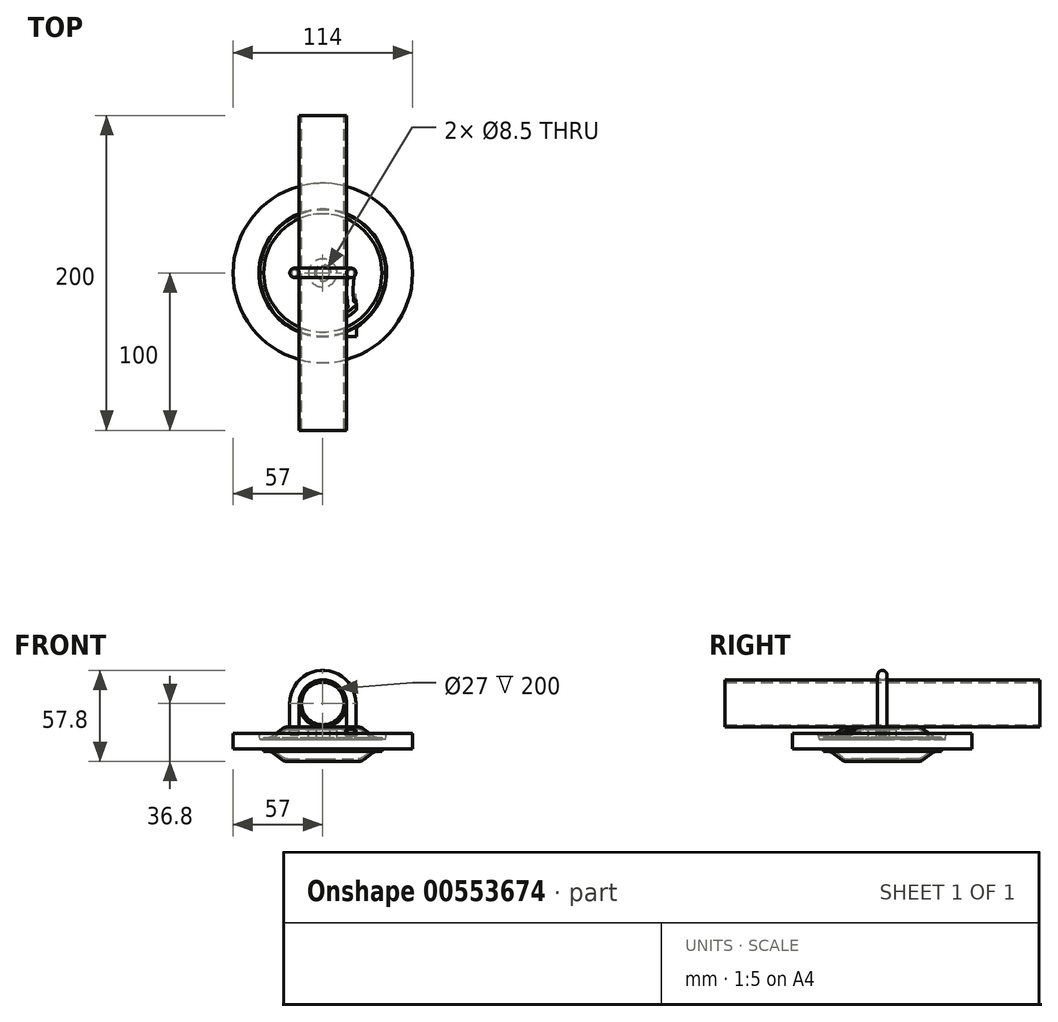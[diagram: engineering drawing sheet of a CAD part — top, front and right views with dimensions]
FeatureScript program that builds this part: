
annotation { "Feature Type Name" : "Feature", "Feature Type Description" : "" }
export const myFeature = defineFeature(function(context is Context, id is Id, definition is map)
    precondition{}
    {
        {
            assignVariable(context, id + "F0", {"name" : "ClampBolzen", "anyValue" : 4});
        }
        {
            var Q0;
            Q0=qCreatedBy(makeId("Front.planeOp"),FACE);
            var sketch = newSketch(context, id + "F1", { "sketchPlane" : qUnion([Q0])});
            skLineSegment(sketch, "E0", {"start": v(0, 0) * mm, "end": v(0, 76.33) * mm, "construction": true});
            skLineSegment(sketch, "E1", {"start": v(0, 0) * mm, "end": v(40, 0) * mm});
            skLineSegment(sketch, "E2", {"start": v(40, 0) * mm, "end": v(40.48, 3.9) * mm});
            skLineSegment(sketch, "E3", {"start": v(40.48, 3.9) * mm, "end": v(57, 3.9) * mm});
            skLineSegment(sketch, "E4", {"start": v(57, 3.9) * mm, "end": v(57, -6) * mm});
            skLineSegment(sketch, "E5", {"start": v(57, -6) * mm, "end": v(0, -6) * mm});
            skLineSegment(sketch, "E6", {"start": v(0, -6) * mm, "end": v(0, 0) * mm});
            skPoint(sketch, "E7", {"position": v(0, -3) * mm});
            skSolve(sketch);
        }
        {
            var Q0;
            Q0=qSketchRegion(id+"F1",true);
            var Q1;
            Q1=sQuery(id+"F1.wireOp",EDGE,"E0");
            revolve(context, id + "F2", {"entities" : qUnion([Q0]), "axis" : qUnion([Q1]), "revolveType" : RevolveType.FULL});
        }
        {
            var Q0;
            Q0=qCreatedBy(makeId("Front.planeOp"),FACE);
            var sketch = newSketch(context, id + "F3", { "sketchPlane" : qUnion([Q0])});
            skCircle(sketch, "E8", {"center": v(0, 22.9) * mm, "radius": 15 * mm});
            skCircle(sketch, "E9", {"center": v(0, 22.9) * mm, "radius": 13.5 * mm});
            skSolve(sketch);
        }
        {
            var Q0;
            Q0=qSketchRegion(id+"F3",true);
            extrude(context, id + "F4", {"entities" : qUnion([Q0]), "endBound" : BoundingType.SYMMETRIC, "depth" : 200 * mm, "offsetDistance" : 25 * mm});
        }
        {
            var Q0;
            Q0=qCreatedBy(makeId("Front.planeOp"),FACE);
            var sketch = newSketch(context, id + "F5", { "sketchPlane" : qUnion([Q0])});
            skLineSegment(sketch, "E10", {"start": v(0, -22.63) * mm, "end": v(0, 22.63) * mm, "construction": true});
            skLineSegment(sketch, "E11", {"start": v(4.25, 7.9) * mm, "end": v(24.5, 7.9) * mm});
            skLineSegment(sketch, "E12", {"start": v(24.5, 7.9) * mm, "end": v(33, 1.5) * mm});
            skLineSegment(sketch, "E13", {"start": v(33, 1.5) * mm, "end": v(37.5, 1.5) * mm});
            skLineSegment(sketch, "E14.0", {"start": v(32.5, 0) * mm, "end": v(37.5, 0) * mm});
            skLineSegment(sketch, "E14.1", {"start": v(24, 6.4) * mm, "end": v(32.5, 0) * mm});
            skLineSegment(sketch, "E14.2", {"start": v(4.25, 6.4) * mm, "end": v(24, 6.4) * mm});
            skLineSegment(sketch, "E15", {"start": v(37.5, 1.5) * mm, "end": v(37.5, 0) * mm});
            skLineSegment(sketch, "E16", {"start": v(15, 7.9) * mm, "end": v(15, 25.1) * mm, "construction": true});
            skLineSegment(sketch, "E17", {"start": v(4.25, 7.9) * mm, "end": v(4.25, 6.4) * mm});
            skSolve(sketch);
        }
        {
            var Q0;
            Q0=makeQuery(id+"F5.imprint","IMPRINT",FACE,{"disambiguationData":[TD([[makeQuery(id+"F5.imprint","IMPRINT",EDGE,{"derivedFrom":sQuery(id+"F5.wireOp",EDGE,"E11")}),-1.0]])]});
            var Q1;
            Q1=sQuery(id+"F5.wireOp",EDGE,"E10");
            revolve(context, id + "F6", {"entities" : qUnion([Q0]), "axis" : qUnion([Q1]), "revolveType" : RevolveType.FULL});
        }
        {
            var Q0;
            Q0=makeQuery(id+"F6.opRevolve","SWEPT_FACE",FACE,{"disambiguationData":[OSD([sQuery(id+"F5.wireOp",EDGE,"E12")])]});
            var Q1;
            Q1=makeQuery(id+"F6.opRevolve","SWEPT_FACE",FACE,{"disambiguationData":[OSD([sQuery(id+"F5.wireOp",EDGE,"E14.1")])]});
            fillet(context, id + "F7", {"entities" : qUnion([Q0, Q1]), "radius" : 5 * mm, "tangentPropagation" : true, "allowEdgeOverflow" : false});
        }
        {
            var Q0;
            Q0=sQuery(id+"F1.wireOp",VERTEX,"E7");
            var Q1;
            Q1=sQuery(id+"F1.wireOp",EDGE,"E6");
            cPlane(context, id + "F8", {"entities" : qUnion([Q0, Q1]), "cplaneType" : CPlaneType.LINE_POINT, "offset" : 25 * mm, "width" : 150 * mm, "height" : 150 * mm});
        }
        {
            var Q0;
            Q0=makeQuery(id+"F6.opRevolve","SWEPT_BODY",BODY,{"disambiguationData":[OSD([sQuery(id+"F5.wireOp",EDGE,"E11"),sQuery(id+"F5.wireOp",EDGE,"E12"),sQuery(id+"F5.wireOp",EDGE,"E13"),sQuery(id+"F5.wireOp",EDGE,"E14.0"),sQuery(id+"F5.wireOp",EDGE,"E14.1"),sQuery(id+"F5.wireOp",EDGE,"E14.2"),sQuery(id+"F5.wireOp",EDGE,"E15"),sQuery(id+"F5.wireOp",EDGE,"E17")])]});
            var Q1;
            Q1=qCreatedBy(id+"F8.planeOp",FACE);
            mirror(context, id + "F9", {"entities" : qUnion([Q0]), "mirrorPlane" : qUnion([Q1])});
        }
        {
            var Q0;
            Q0=makeQuery(id+"F6.opRevolve","SWEPT_FACE",FACE,{"disambiguationData":[OSD([sQuery(id+"F5.wireOp",EDGE,"E14.2")])]});
            var sketch = newSketch(context, id + "F10", { "sketchPlane" : qUnion([Q0])});
            skCircle(sketch, "E18", {"center": v(0, 0) * mm, "radius": 9 * mm});
            skCircle(sketch, "E19.0", {"center": v(0, 0) * mm, "radius": 4.25 * mm});
            skSolve(sketch);
        }
        {
            var Q0;
            Q0 = qSketchRegion(id + "F10", true);
            extrude(context, id + "F11", {"entities" : qUnion([Q0]), "operationType" : NewBodyOperationType.ADD, "depth" : 6 * mm, "offsetDistance" : 25 * mm});
        }
        {
            var Q0;
            Q0=makeQuery(id+"F11.opExtrude","CAP_EDGE",EDGE,{"disambiguationData":[OSD([sQuery(id+"F10.wireOp",EDGE,"E18")])],"isStart":false});
            fillet(context, id + "F12", {"entities" : qUnion([Q0]), "radius" : 1 * mm, "tangentPropagation" : true, "allowEdgeOverflow" : false});
        }
        {
            var Q0;
            Q0=makeQuery(id+"F11.boolean.opBoolean","MERGE",FACE,{"derivedFrom":[makeQuery(id+"F6.opRevolve","SWEPT_FACE",FACE,{"disambiguationData":[OSD([sQuery(id+"F5.wireOp",EDGE,"E17")])]}),makeQuery(id+"F11.opExtrude","SWEPT_FACE",FACE,{"disambiguationData":[OSD([sQuery(id+"F10.wireOp",EDGE,"E19.0")])]})]});
            chamfer(context, id + "F13", {"entities" : qUnion([Q0]), "width" : 1 * mm, "tangentPropagation" : true});
        }
        {
            var Q0;
            Q0=qCreatedBy(makeId("Front.planeOp"),FACE);
            var sketch = newSketch(context, id + "F14", { "sketchPlane" : qUnion([Q0])});
            skCircle(sketch, "E20.0", {"center": v(0, 22.9) * mm, "radius": 15 * mm, "construction": true});
            skLineSegment(sketch, "E21", {"start": v(-15, 6.4) * mm, "end": v(-15, 22.9) * mm, "construction": true});
            skLineSegment(sketch, "E22", {"start": v(-18, 22.9) * mm, "end": v(-18, 7.9) * mm});
            skArc(sketch, "E23", {"start": v(-18, 22.9) * mm, "mid": v(0, 40.9) * mm, "end": v(18, 22.9) * mm});
            skLineSegment(sketch, "E24", {"start": v(18, 22.9) * mm, "end": v(18, 7.9) * mm});
            skSolve(sketch);
        }
        {
            var Q0;
            Q0=makeQuery(id+"F6.opRevolve","SWEPT_FACE",FACE,{"disambiguationData":[OSD([sQuery(id+"F5.wireOp",EDGE,"E11")])]});
            var sketch = newSketch(context, id + "F15", { "sketchPlane" : qUnion([Q0])});
            skPoint(sketch, "E25.0", {"position": v(18, 0) * mm});
            skPoint(sketch, "E26.0", {"position": v(-18, 0) * mm});
            skSolve(sketch);
        }
        {
            var Q0;
            Q0=sQuery(id+"F15.wireOp",VERTEX,"E26.0");
            var Q1;
            Q1=sQuery(id+"F15.wireOp",VERTEX,"E25.0");
            var Q2;
            Q2=makeQuery(id+"F6.opRevolve","SWEPT_BODY",BODY,{"disambiguationData":[OSD([sQuery(id+"F5.wireOp",EDGE,"E11"),sQuery(id+"F5.wireOp",EDGE,"E12"),sQuery(id+"F5.wireOp",EDGE,"E13"),sQuery(id+"F5.wireOp",EDGE,"E14.0"),sQuery(id+"F5.wireOp",EDGE,"E14.1"),sQuery(id+"F5.wireOp",EDGE,"E14.2"),sQuery(id+"F5.wireOp",EDGE,"E15"),sQuery(id+"F5.wireOp",EDGE,"Ff8F4mr3-Qqlt-WCVs-9Xkp-wYiXQ1rS5Auy")])]});
            hole(context, id + "F16", {"style" : HoleStyle.SIMPLE, "endStyle" : HoleEndStyle.THROUGH, "holeDiameter" : (getVariable(context, 'ClampBolzen')) * mm, "isTappedThrough" : true, "tappedDepth" : 12 * mm, "tapClearance" : 3, "locations" : qUnion([Q0, Q1]), "scope" : qUnion([Q2])});
        }
        {
            var Q0;
            Q0=sQuery(id+"F14.wireOp",VERTEX,"E22.end");
            var Q1;
            Q1=sQuery(id+"F14.wireOp",EDGE,"E22");
            cPlane(context, id + "F17", {"entities" : qUnion([Q0, Q1]), "cplaneType" : CPlaneType.LINE_POINT, "offset" : 25 * mm, "width" : 150 * mm, "height" : 150 * mm});
        }
        {
            var Q0;
            Q0=qCreatedBy(id+"F17.planeOp",FACE);
            var sketch = newSketch(context, id + "F18", { "sketchPlane" : qUnion([Q0])});
            skCircle(sketch, "E27", {"center": v(-18, 0) * mm, "radius": 3 * mm});
            skSolve(sketch);
        }
        {
            var Q0;
            Q0 = qSketchRegion(id + "F18", true);
            var Q1;
            Q1 = qConstructionFilter(qBodyType(qCreatedBy(id + "F14" ,EDGE), BodyType.WIRE), ConstructionObject.NO);
            sweep(context, id + "F19", {"profiles" : qUnion([Q0]), "path" : qUnion([Q1])});
        }
        {
            var Q0;
            Q0=qCreatedBy(makeId("Front.planeOp"),FACE);
            var sketch = newSketch(context, id + "F20", { "sketchPlane" : qUnion([Q0])});
            skLineSegment(sketch, "E28", {"start": v(-20, 7.9) * mm, "end": v(-20, 5.9) * mm});
            skLineSegment(sketch, "E29", {"start": v(-20, 5.9) * mm, "end": v(-21, 5.9) * mm});
            skLineSegment(sketch, "E30", {"start": v(-21, 5.9) * mm, "end": v(-21, 2.9) * mm});
            skLineSegment(sketch, "E31", {"start": v(-21, 2.9) * mm, "end": v(-18, 2.9) * mm});
            skLineSegment(sketch, "E32", {"start": v(-18, 2.9) * mm, "end": v(-18, 7.9) * mm});
            skLineSegment(sketch, "E33", {"start": v(-18, 7.9) * mm, "end": v(-20, 7.9) * mm});
            skLineSegment(sketch, "E34", {"start": v(-18, 7.9) * mm, "end": v(-18, 2.08) * mm, "construction": true});
            skPoint(sketch, "E35", {"position": v(-21, 7.9) * mm});
            skLineSegment(sketch, "E36.0", {"start": v(-15, 7.9) * mm, "end": v(-21, 7.9) * mm, "construction": true});
            skSolve(sketch);
        }
        {
            var Q0;
            Q0=makeQuery(id+"F20.imprint","IMPRINT",FACE,{"disambiguationData":[TD([[makeQuery(id+"F20.imprint","IMPRINT",EDGE,{"derivedFrom":sQuery(id+"F20.wireOp",EDGE,"E28")}),1.0]])]});
            var Q1;
            Q1=sQuery(id+"F20.wireOp",EDGE,"E34");
            revolve(context, id + "F21", {"operationType" : NewBodyOperationType.ADD, "entities" : qUnion([Q0]), "axis" : qUnion([Q1]), "revolveType" : RevolveType.FULL});
        }
        {
            var Q0;
            Q0=makeQuery(id+"F21.opRevolve","SWEPT_EDGE",EDGE,{"disambiguationData":[OSD([sQuery(id+"F20.wireOp",EDGE,"E30"),sQuery(id+"F20.wireOp",EDGE,"E31")])]});
            var Q1;
            Q1=makeQuery(id+"FYgZe8NV0yxJnGN_4.1.F21.opRevolve","SWEPT_FACE",FACE,{"disambiguationData":[OSD([sQuery(id+"F20.wireOp",EDGE,"E31")])]});
            chamfer(context, id + "F22", {"entities" : qUnion([Q0, Q1]), "width" : .5 * mm, "tangentPropagation" : true});
        }
        {
            var Q0;
            Q0=qCreatedBy(makeId("Front.planeOp"),FACE);
            var sketch = newSketch(context, id + "F23", { "sketchPlane" : qUnion([Q0])});
            skLineSegment(sketch, "E37", {"start": v(20, 7.9) * mm, "end": v(20, 6.2) * mm});
            skLineSegment(sketch, "E38", {"start": v(21, 5.9) * mm, "end": v(21, 3.4) * mm, "construction": true});
            skLineSegment(sketch, "E39.0", {"start": v(21.2, 2.4) * mm, "end": v(18, 2.4) * mm});
            skLineSegment(sketch, "E40", {"start": v(20.3, 5.9) * mm, "end": v(21.2, 5.9) * mm});
            skLineSegment(sketch, "E41", {"start": v(18, 7.9) * mm, "end": v(20, 7.9) * mm});
            skPoint(sketch, "E42.visualSharp", {"position": v(20, 5.9) * mm});
            skArc(sketch, "E42.filletArc", {"start": v(20, 6.2) * mm, "mid": v(20.09, 5.99) * mm, "end": v(20.3, 5.9) * mm});
            skLineSegment(sketch, "E43", {"start": v(21.5, 5.6) * mm, "end": v(21.5, 2.7) * mm});
            skLineSegment(sketch, "E44", {"start": v(18, 7.9) * mm, "end": v(18, 2.4) * mm, "construction": true});
            skPoint(sketch, "E45.visualSharp", {"position": v(21.5, 2.4) * mm});
            skArc(sketch, "E45.filletArc", {"start": v(21.2, 2.4) * mm, "mid": v(21.41, 2.49) * mm, "end": v(21.5, 2.7) * mm});
            skPoint(sketch, "E46.visualSharp", {"position": v(21.5, 5.9) * mm});
            skArc(sketch, "E46.filletArc", {"start": v(21.5, 5.6) * mm, "mid": v(21.41, 5.81) * mm, "end": v(21.2, 5.9) * mm});
            skArc(sketch, "E47.MirrorCS", {"start": v(14.8, 2.4) * mm, "mid": v(14.59, 2.49) * mm, "end": v(14.5, 2.7) * mm});
            skArc(sketch, "E48.MirrorCS", {"start": v(16, 6.2) * mm, "mid": v(15.91, 5.99) * mm, "end": v(15.7, 5.9) * mm});
            skLineSegment(sketch, "E49.MirrorCS", {"start": v(16, 7.9) * mm, "end": v(16, 6.2) * mm});
            skPoint(sketch, "E50.MirrorP", {"position": v(14.5, 5.9) * mm});
            skArc(sketch, "E51.MirrorCS", {"start": v(14.5, 5.6) * mm, "mid": v(14.59, 5.81) * mm, "end": v(14.8, 5.9) * mm});
            skLineSegment(sketch, "E52.MirrorCS", {"start": v(15, 5.9) * mm, "end": v(15, 3.4) * mm, "construction": true});
            skLineSegment(sketch, "E53.MirrorCS", {"start": v(14.5, 5.6) * mm, "end": v(14.5, 2.7) * mm});
            skLineSegment(sketch, "E54.MirrorCS", {"start": v(14.8, 2.4) * mm, "end": v(18, 2.4) * mm});
            skPoint(sketch, "E55.MirrorP", {"position": v(16, 5.9) * mm});
            skPoint(sketch, "E56.MirrorP", {"position": v(14.5, 2.4) * mm});
            skLineSegment(sketch, "E57.MirrorCS", {"start": v(18, 7.9) * mm, "end": v(16, 7.9) * mm});
            skLineSegment(sketch, "E58.MirrorCS", {"start": v(15.7, 5.9) * mm, "end": v(14.8, 5.9) * mm});
            skSolve(sketch);
        }
        {
            var Q0;
            Q0=makeQuery(id+"F6.opRevolve","SWEPT_FACE",FACE,{"disambiguationData":[OSD([sQuery(id+"F5.wireOp",EDGE,"E11")])]});
            var sketch = newSketch(context, id + "F24", { "sketchPlane" : qUnion([Q0])});
            skPoint(sketch, "E59", {"position": v(17.1, -10.26) * mm});
            skLineSegment(sketch, "E60", {"start": v(18, 0) * mm, "end": v(18, 0) * mm});
            skLineSegment(sketch, "E61", {"start": v(17.9, -1.94) * mm, "end": v(17.1, -10.26) * mm});
            skLineSegment(sketch, "E62", {"start": v(17, -11.23) * mm, "end": v(18, -11.23) * mm, "construction": true});
            skLineSegment(sketch, "E63.MirrorCS", {"start": v(18, -22.46) * mm, "end": v(18, -22.46) * mm});
            skLineSegment(sketch, "E64.MirrorCS", {"start": v(17.9, -20.52) * mm, "end": v(17.1, -12.2) * mm});
            skPoint(sketch, "E65.visualSharp", {"position": v(18, -21.49) * mm});
            skArc(sketch, "E65.filletArc", {"start": v(18, -22.46) * mm, "mid": v(17.98, -21.49) * mm, "end": v(17.9, -20.52) * mm});
            skPoint(sketch, "E66.visualSharp", {"position": v(18, -0.97) * mm});
            skArc(sketch, "E66.filletArc", {"start": v(17.9, -1.94) * mm, "mid": v(17.98, -0.97) * mm, "end": v(18, 0) * mm});
            skPoint(sketch, "E67.visualSharp", {"position": v(17, -11.23) * mm});
            skArc(sketch, "E67.filletArc", {"start": v(17.1, -10.26) * mm, "mid": v(17.05, -11.23) * mm, "end": v(17.1, -12.2) * mm});
            skLineSegment(sketch, "E68", {"start": v(18, -22.46) * mm, "end": v(18, -40.46) * mm});
            skSolve(sketch);
        }
        {
            var Q0;
            Q0 = qSketchRegion(id + "F23", true);
            var Q1;
            Q1 = qConstructionFilter(qBodyType(qCreatedBy(id + "F24" ,EDGE), BodyType.WIRE), ConstructionObject.NO);
            sweep(context, id + "F25", {"operationType" : NewBodyOperationType.REMOVE, "profiles" : qUnion([Q0]), "path" : qUnion([Q1]), "keepProfileOrientation" : true});
        }
    });
